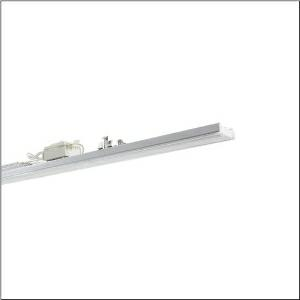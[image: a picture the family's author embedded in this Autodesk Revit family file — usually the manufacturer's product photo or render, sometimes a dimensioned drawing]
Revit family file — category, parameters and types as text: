
# Revit family: licross_r__11_recessed_mo_51tl12dn4axg_bf66
name_source: partatom
category: Lighting Fixtures
units: mm (PartAtom-declared; Revit-internal decimal feet)

## family parameters
Cut with Voids When Loaded = No
Host = Face
Light Source = No
Part Type = Normal
Room Calculation Point = No
Round Connector Dimension = Use Diameter
Shared = No

## types (1)
- --- (1 x LED, 10240 lm, 56.7 W, 4000K)
    Apparent Load = 57 VA
    CIE Flux Codes = 67 92 99 100 100
    Color Rendering = 80
    Color Temperature = 4000K
    Default Elevation = 1800 mm
    Description = Licross® 11 Recessed MO, luminaire insert, of sheet steel, coil coated, white, length: 1.500mm, width: 66mm, height: 67mm, LED rated luminous flux: 10.240lm, light colour: 840, control gear: DALI 2, with plug, 5-pole, with phase selection, mains connection: 220..240V, AC, 50/60Hz, rated input power: 57W, halogen-free wiring, primary optical cover: cover, of PMMA, light emission: direct distribution, primary light characteristic: symmetric, protection rating (complete): IP40, insulation class (complete): insulation class I (protective earthing), certification: CE, ENEC, VDE, UKCA, protection symbol: D if used in an environment without relevant dust loads with corresponding accessories, impact resistance: IK06, permissible ambient temperature for indoor applications: -25..+35°C, corresponds to IFS (International Featured Standards) requirements for safety and quality in the food industry, reducing of maximum allowable ambient temperature of 5°C with ceiling mounting, LABS conformity tested according to VDMA 24364:2018-05, packaging unit: 1 piece
    Height = 58 mm
    Lamp = 1 x LED
    Lamp Light Flux = 10240 lm
    Lamp Power = 56.7 W
    Lamp count = 1
    Length = 1500 mm
    Luminous efficacy = 181 lm/W
    Manufacturer = Siteco
    ModVariant = No
    Model = 51TL12DN4AXG
    Mounting Place = Ceiling
    Mounting Type = Pendant
    Number of Poles = 1
    OnlyDefault = Yes
    Power Factor = 1
    Product Name = Licross® 11 Recessed MO
    Product group = luminaire insert
    ProductGroupID = 902
    Protection Class = Protection class I
    Protection Degree = IP 40
    RLX_Detail_Level = 1
    RLX_Emergency_Light_Flux = 0 lm
    RLX_Emergency_Type = 0
    RLX_Emergency_Type_DB = No
    RlxData = <blob elided: 24317 chars, md5=d5bff07f>
    Socket = socket
    Standby Power = 0 W
    System Light Flux = 10240 lm
    System Power = 57 W
    Type Comments = factory setting: luminous flux: 100 % | dim-lin: 254 | 378 mA
    Type Image = l_1296930.jpg
    URL = http://relux.com
    VarID = @adj_100352
    Voltage = 0 V
    Weight = 0.00 kg
    Width = 66 mm

## geometry (parser evidence)
native form markers: Blend x4, Sweep x11
no freeform markers — native parametric forms only
